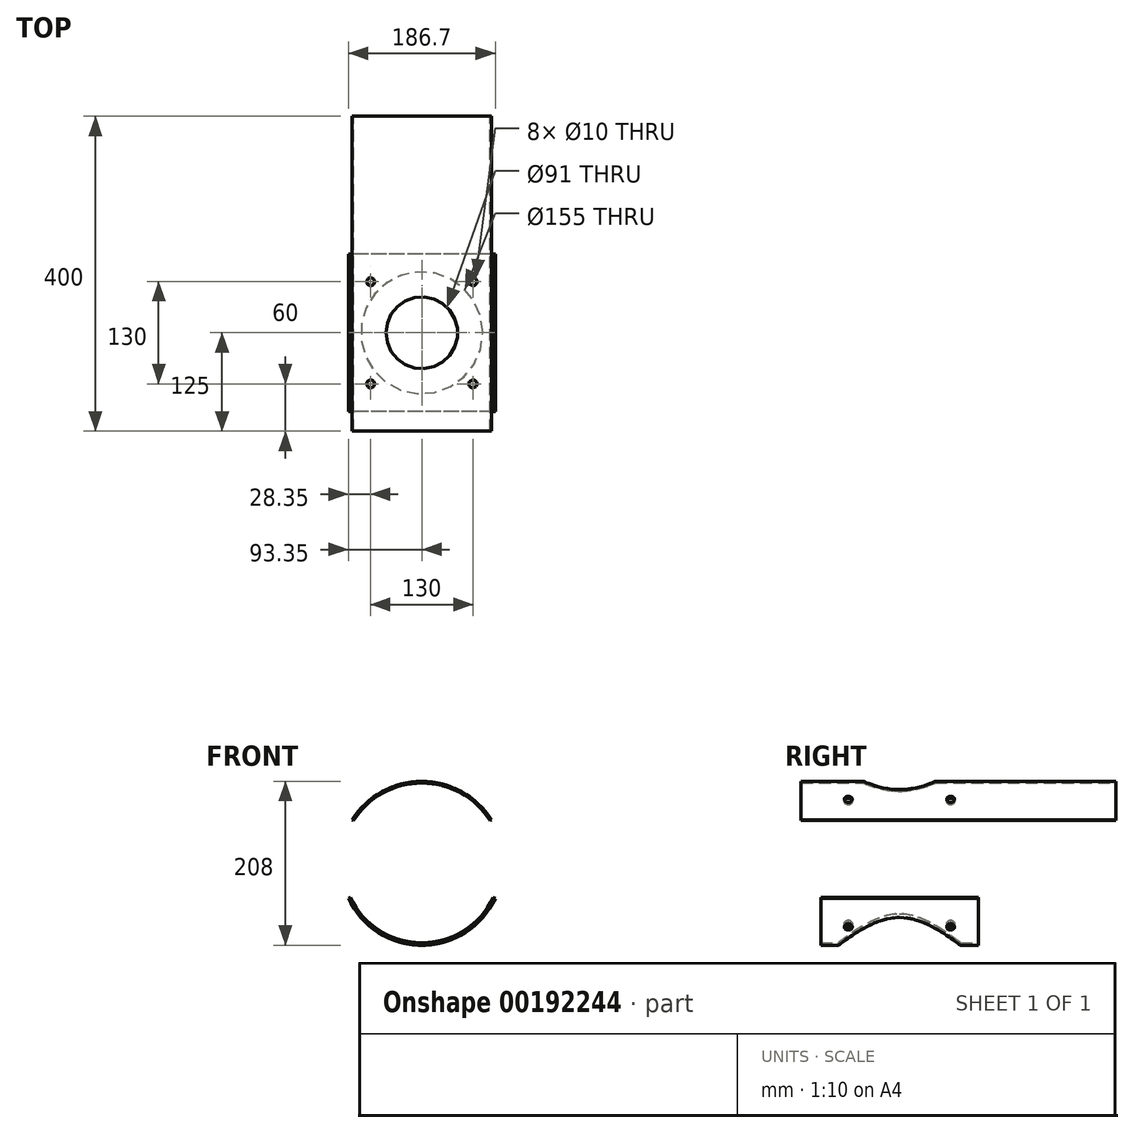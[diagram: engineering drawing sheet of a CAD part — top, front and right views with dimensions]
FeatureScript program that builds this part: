
annotation { "Feature Type Name" : "Feature", "Feature Type Description" : "" }
export const myFeature = defineFeature(function(context is Context, id is Id, definition is map)
    precondition{}
    {
        {
            var Q0;
            Q0=qCreatedBy(makeId("Right.planeOp"),FACE);
            var sketch = newSketch(context, id + "F0", { "sketchPlane" : qUnion([Q0])});
            skLineSegment(sketch, "E0.bottom", {"start": v(-125, 105) * mm, "end": v(275, 105) * mm});
            skLineSegment(sketch, "E0.top", {"start": v(-125, 103) * mm, "end": v(275, 103) * mm});
            skLineSegment(sketch, "E0.left", {"start": v(-125, 105) * mm, "end": v(-125, 103) * mm});
            skLineSegment(sketch, "E0.right", {"start": v(275, 105) * mm, "end": v(275, 103) * mm});
            skSolve(sketch);
        }
        {
            var Q0;
            Q0=qCreatedBy(makeId("Top.planeOp"),FACE);
            var sketch = newSketch(context, id + "F1", { "sketchPlane" : qUnion([Q0])});
            skLineSegment(sketch, "E1", {"start": v(0, 119.38) * mm, "end": v(0, -126.03) * mm});
            skSolve(sketch);
        }
        {
            var Q0;
            Q0=makeQuery(id+"F0.imprint","IMPRINT",FACE,{"disambiguationData":[TD([[makeQuery(id+"F0.imprint","IMPRINT",EDGE,{"derivedFrom":sQuery(id+"F0.wireOp",EDGE,"E0.bottom")}),-1.0]])]});
            var Q1;
            Q1=sQuery(id+"F1.wireOp",EDGE,"E1");
            revolve(context, id + "F2", {"entities" : qUnion([Q0]), "axis" : qUnion([Q1]), "revolveType" : RevolveType.SYMMETRIC, "angle" : 115 * degree});
        }
        {
            var Q0;
            Q0=qCreatedBy(makeId("Top.planeOp"),FACE);
            var sketch = newSketch(context, id + "F3", { "sketchPlane" : qUnion([Q0])});
            skCircle(sketch, "E2", {"center": v(0, 0) * mm, "radius": 45.5 * mm});
            skSolve(sketch);
        }
        {
            var Q0;
            Q0=makeQuery(id+"F3.imprint","IMPRINT",FACE,{"disambiguationData":[TD([[makeQuery(id+"F3.imprint","IMPRINT",EDGE,{"derivedFrom":sQuery(id+"F3.wireOp",EDGE,"E2")}),1.0]])]});
            extrude(context, id + "F4", {"entities" : qUnion([Q0]), "operationType" : NewBodyOperationType.REMOVE, "depth" : 161 * mm});
        }
        {
            var Q0;
            Q0=qCreatedBy(makeId("Top.planeOp"),FACE);
            var sketch = newSketch(context, id + "F5", { "sketchPlane" : qUnion([Q0])});
            skCircle(sketch, "E3", {"center": v(65, 65) * mm, "radius": 5 * mm});
            skCircle(sketch, "E4", {"center": v(65, -65) * mm, "radius": 5 * mm});
            skCircle(sketch, "E5", {"center": v(-65, 65) * mm, "radius": 5 * mm});
            skCircle(sketch, "E6", {"center": v(-65, -65) * mm, "radius": 5 * mm});
            skSolve(sketch);
        }
        {
            var Q0;
            Q0=makeQuery(id+"F5.imprint","IMPRINT",FACE,{"disambiguationData":[TD([[makeQuery(id+"F5.imprint","IMPRINT",EDGE,{"derivedFrom":sQuery(id+"F5.wireOp",EDGE,"E5")}),1.0]])]});
            extrude(context, id + "F6", {"entities" : qUnion([Q0]), "operationType" : NewBodyOperationType.REMOVE, "depth" : 136 * mm});
        }
        {
            var Q0;
            Q0=makeQuery(id+"F5.imprint","IMPRINT",FACE,{"disambiguationData":[TD([[makeQuery(id+"F5.imprint","IMPRINT",EDGE,{"derivedFrom":sQuery(id+"F5.wireOp",EDGE,"E6")}),1.0]])]});
            var Q1;
            Q1=makeQuery(id+"F5.imprint","IMPRINT",FACE,{"disambiguationData":[TD([[makeQuery(id+"F5.imprint","IMPRINT",EDGE,{"derivedFrom":sQuery(id+"F5.wireOp",EDGE,"E4")}),1.0]])]});
            var Q2;
            Q2=makeQuery(id+"F5.imprint","IMPRINT",FACE,{"disambiguationData":[TD([[makeQuery(id+"F5.imprint","IMPRINT",EDGE,{"derivedFrom":sQuery(id+"F5.wireOp",EDGE,"E3")}),1.0]])]});
            var Q3;
            Q3=sQuery(id+"F5.wireOp",EDGE,"E6");
            var Q4;
            Q4=sQuery(id+"F5.wireOp",EDGE,"E4");
            var Q5;
            Q5=sQuery(id+"F5.wireOp",EDGE,"E3");
            extrude(context, id + "F7", {"entities" : qUnion([Q0, Q1, Q2]), "operationType" : NewBodyOperationType.REMOVE, "surfaceEntities" : qUnion([Q3, Q4, Q5]), "endBound" : BoundingType.SYMMETRIC, "depth" : 220 * mm});
        }
        {
            var Q0;
            Q0=qCreatedBy(makeId("Right.planeOp"),FACE);
            var sketch = newSketch(context, id + "F8", { "sketchPlane" : qUnion([Q0])});
            skLineSegment(sketch, "E7.bottom", {"start": v(-100, -100) * mm, "end": v(100, -100) * mm});
            skLineSegment(sketch, "E7.top", {"start": v(-100, -103) * mm, "end": v(100, -103) * mm});
            skLineSegment(sketch, "E7.left", {"start": v(-100, -100) * mm, "end": v(-100, -103) * mm});
            skLineSegment(sketch, "E7.right", {"start": v(100, -100) * mm, "end": v(100, -103) * mm});
            skSolve(sketch);
        }
        {
            var Q0;
            Q0=makeQuery(id+"F8.imprint","IMPRINT",FACE,{"disambiguationData":[TD([[makeQuery(id+"F8.imprint","IMPRINT",EDGE,{"derivedFrom":sQuery(id+"F8.wireOp",EDGE,"E7.bottom")}),-1.0]])]});
            var Q1;
            Q1=sQuery(id+"F1.wireOp",EDGE,"E1");
            revolve(context, id + "F9", {"entities" : qUnion([Q0]), "axis" : qUnion([Q1]), "revolveType" : RevolveType.SYMMETRIC, "angle" : 130 * degree});
        }
        {
            var Q0;
            Q0=qCreatedBy(makeId("Top.planeOp"),FACE);
            var sketch = newSketch(context, id + "F10", { "sketchPlane" : qUnion([Q0])});
            skCircle(sketch, "E8", {"center": v(0, 0) * mm, "radius": 77.5 * mm});
            skSolve(sketch);
        }
        {
            var Q0;
            Q0=makeQuery(id+"F10.imprint","IMPRINT",FACE,{"disambiguationData":[TD([[makeQuery(id+"F10.imprint","IMPRINT",EDGE,{"derivedFrom":sQuery(id+"F10.wireOp",EDGE,"E8")}),1.0]])]});
            extrude(context, id + "F11", {"entities" : qUnion([Q0]), "operationType" : NewBodyOperationType.REMOVE, "oppositeDirection" : true, "depth" : 132.7 * mm});
        }
        {
            var Q0;
            Q0=makeQuery(id+"F5.imprint","IMPRINT",FACE,{"disambiguationData":[TD([[makeQuery(id+"F5.imprint","IMPRINT",EDGE,{"derivedFrom":sQuery(id+"F5.wireOp",EDGE,"E5")}),1.0]])]});
            var Q1;
            Q1=makeQuery(id+"F5.imprint","IMPRINT",FACE,{"disambiguationData":[TD([[makeQuery(id+"F5.imprint","IMPRINT",EDGE,{"derivedFrom":sQuery(id+"F5.wireOp",EDGE,"E6")}),1.0]])]});
            var Q2;
            Q2=makeQuery(id+"F5.imprint","IMPRINT",FACE,{"disambiguationData":[TD([[makeQuery(id+"F5.imprint","IMPRINT",EDGE,{"derivedFrom":sQuery(id+"F5.wireOp",EDGE,"E4")}),1.0]])]});
            var Q3;
            Q3=makeQuery(id+"F5.imprint","IMPRINT",FACE,{"disambiguationData":[TD([[makeQuery(id+"F5.imprint","IMPRINT",EDGE,{"derivedFrom":sQuery(id+"F5.wireOp",EDGE,"E3")}),1.0]])]});
            extrude(context, id + "F12", {"entities" : qUnion([Q0, Q1, Q2, Q3]), "operationType" : NewBodyOperationType.REMOVE, "oppositeDirection" : true, "depth" : 210 * mm});
        }
    });
